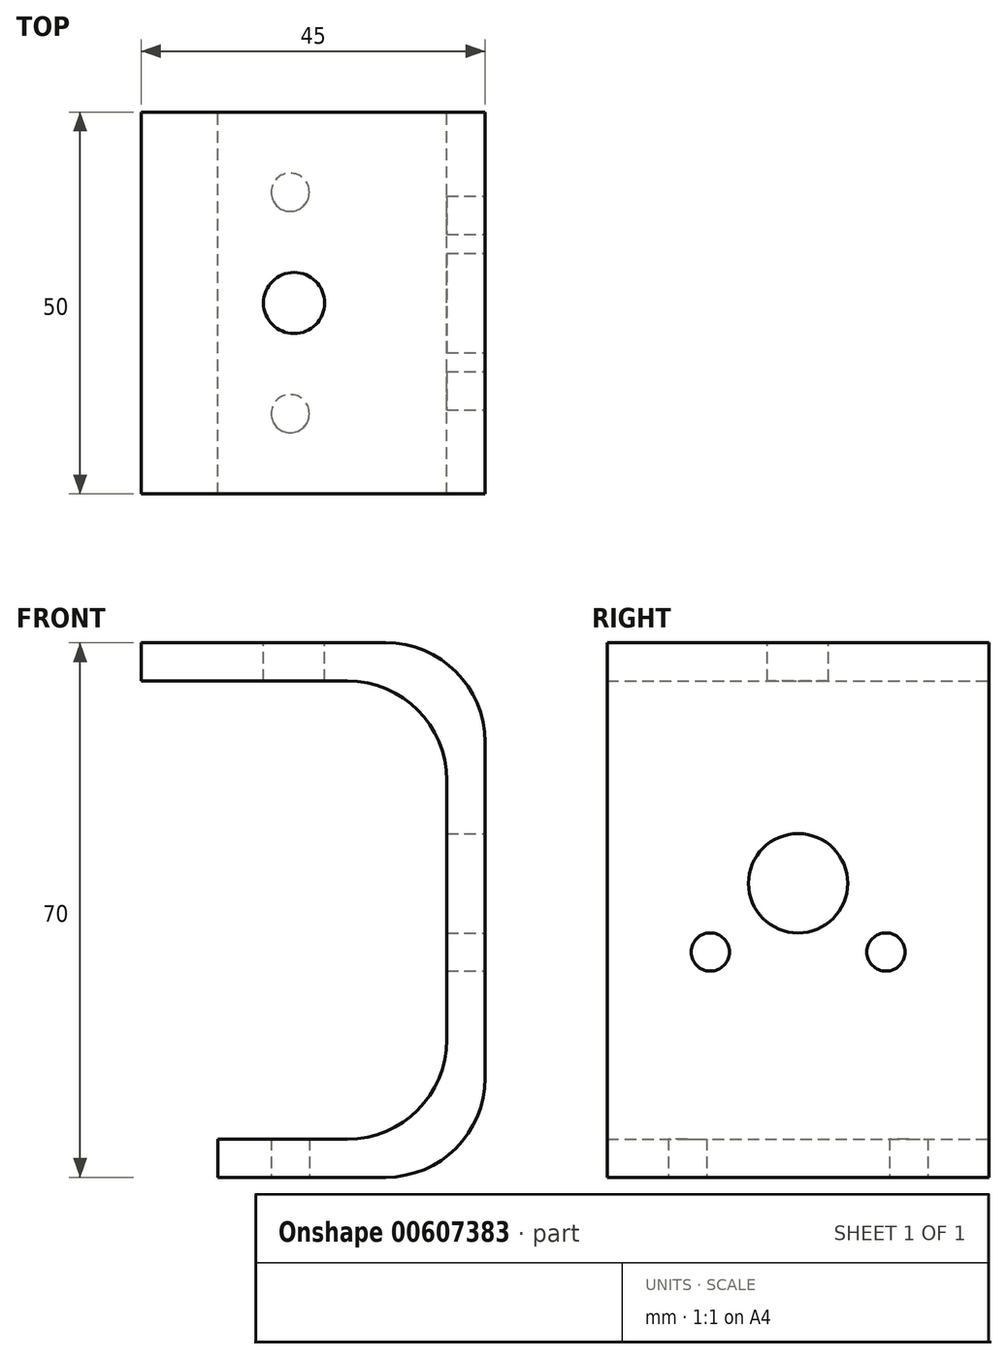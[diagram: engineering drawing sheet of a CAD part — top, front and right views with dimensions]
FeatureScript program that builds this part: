
annotation { "Feature Type Name" : "Feature", "Feature Type Description" : "" }
export const myFeature = defineFeature(function(context is Context, id is Id, definition is map)
    precondition{}
    {
        {
            var Q0;
            Q0=qCreatedBy(makeId("Front.planeOp"),FACE);
            var sketch = newSketch(context, id + "F0", { "sketchPlane" : qUnion([Q0])});
            skLineSegment(sketch, "E0.bottom", {"start": v(7.5, -35) * mm, "end": v(-27.5, -35) * mm});
            skLineSegment(sketch, "E0.top", {"start": v(7.5, 35) * mm, "end": v(-37.5, 35) * mm});
            skLineSegment(sketch, "E0.left", {"start": v(7.5, -35) * mm, "end": v(7.5, 35) * mm});
            skPoint(sketch, "E0.middle", {"position": v(0, 0) * mm});
            skLineSegment(sketch, "E1.bottom", {"start": v(-37.5, 30) * mm, "end": v(2.5, 30) * mm});
            skLineSegment(sketch, "E1.top", {"start": v(-27.5, -30) * mm, "end": v(2.5, -30) * mm});
            skLineSegment(sketch, "E1.right", {"start": v(2.5, 30) * mm, "end": v(2.5, -30) * mm});
            skLineSegment(sketch, "E2", {"start": v(-37.5, 30) * mm, "end": v(-37.5, 35) * mm});
            skLineSegment(sketch, "E3", {"start": v(-27.5, -35) * mm, "end": v(-27.5, -30) * mm});
            skSolve(sketch);
        }
        {
            var Q0;
            {var subQ1=sQuery(id+"F0.wireOp",EDGE,"E0.bottom");Q0=makeQuery(id+"F0.imprint","IMPRINT",FACE,{"disambiguationData":[TD([[makeQuery(id+"F0.imprint","IMPRINT",EDGE,{"derivedFrom":subQ1}),-1.0]])]});}
            extrude(context, id + "F1", {"entities" : qUnion([Q0]), "depth" : 25 * mm, "offsetDistance" : 25 * mm, "hasSecondDirection" : true, "secondDirectionOppositeDirection" : true, "secondDirectionDepth" : 25 * mm});
        }
        {
            var Q0;
            Q0=makeQuery(id+"F1.opExtrude","SWEPT_EDGE",EDGE,{"disambiguationData":[OSD([sQuery(id+"F0.wireOp",EDGE,"E0.top"),sQuery(id+"F0.wireOp",EDGE,"E0.left")])]});
            var Q1;
            Q1=makeQuery(id+"F1.opExtrude","SWEPT_EDGE",EDGE,{"disambiguationData":[OSD([sQuery(id+"F0.wireOp",EDGE,"E0.bottom"),sQuery(id+"F0.wireOp",EDGE,"E0.left")])]});
            var Q2;
            Q2=makeQuery(id+"F1.opExtrude","SWEPT_EDGE",EDGE,{"disambiguationData":[OSD([sQuery(id+"F0.wireOp",EDGE,"E1.top"),sQuery(id+"F0.wireOp",EDGE,"E1.right")])]});
            var Q3;
            Q3=makeQuery(id+"F1.opExtrude","SWEPT_EDGE",EDGE,{"disambiguationData":[OSD([sQuery(id+"F0.wireOp",EDGE,"E1.bottom"),sQuery(id+"F0.wireOp",EDGE,"E1.right")])]});
            fillet(context, id + "F2", {"entities" : qUnion([Q0, Q1, Q2, Q3]), "radius" : 13 * mm, "tangentPropagation" : true, "allowEdgeOverflow" : false});
        }
        {
            var Q0;
            Q0=makeQuery(id+"F1.opExtrude","SWEPT_FACE",FACE,{"disambiguationData":[OSD([sQuery(id+"F0.wireOp",EDGE,"E0.top")])]});
            var sketch = newSketch(context, id + "F3", { "sketchPlane" : qUnion([Q0])});
            skCircle(sketch, "E4", {"center": v(-17.5, 0) * mm, "radius": 4 * mm});
            skSolve(sketch);
        }
        {
            var Q0;
            Q0 = qSketchRegion(id + "F3", true);
            extrude(context, id + "F4", {"entities" : qUnion([Q0]), "operationType" : NewBodyOperationType.REMOVE, "oppositeDirection" : true, "depth" : 10 * mm, "offsetDistance" : 25 * mm});
        }
        {
            var Q0;
            Q0=makeQuery(id+"F1.opExtrude","SWEPT_FACE",FACE,{"disambiguationData":[OSD([sQuery(id+"F0.wireOp",EDGE,"E0.bottom")])]});
            var sketch = newSketch(context, id + "F5", { "sketchPlane" : qUnion([Q0])});
            skCircle(sketch, "E5", {"center": v(-18, -14.5) * mm, "radius": 2.5 * mm});
            skCircle(sketch, "E6.MirrorC", {"center": v(-18, 14.5) * mm, "radius": 2.5 * mm});
            skSolve(sketch);
        }
        {
            var Q0;
            Q0 = qSketchRegion(id + "F5", true);
            extrude(context, id + "F6", {"entities" : qUnion([Q0]), "operationType" : NewBodyOperationType.REMOVE, "oppositeDirection" : true, "depth" : 10 * mm, "offsetDistance" : 25 * mm});
        }
        {
            var Q0;
            Q0=makeQuery(id+"F1.opExtrude","SWEPT_FACE",FACE,{"disambiguationData":[OSD([sQuery(id+"F0.wireOp",EDGE,"E0.left")])]});
            var sketch = newSketch(context, id + "F7", { "sketchPlane" : qUnion([Q0])});
            skLineSegment(sketch, "E7", {"start": v(-25, -5.5) * mm, "end": v(25, -5.5) * mm, "construction": true});
            skCircle(sketch, "E8", {"center": v(11.5, -5.5) * mm, "radius": 2.5 * mm});
            skCircle(sketch, "E9.MirrorC", {"center": v(-11.5, -5.5) * mm, "radius": 2.5 * mm});
            skCircle(sketch, "E10", {"center": v(0, 3.5) * mm, "radius": 6.5 * mm});
            skSolve(sketch);
        }
        {
            var Q0;
            Q0 = qSketchRegion(id + "F7", true);
            extrude(context, id + "F8", {"entities" : qUnion([Q0]), "operationType" : NewBodyOperationType.REMOVE, "oppositeDirection" : true, "depth" : 10 * mm, "offsetDistance" : 25 * mm});
        }
    });
